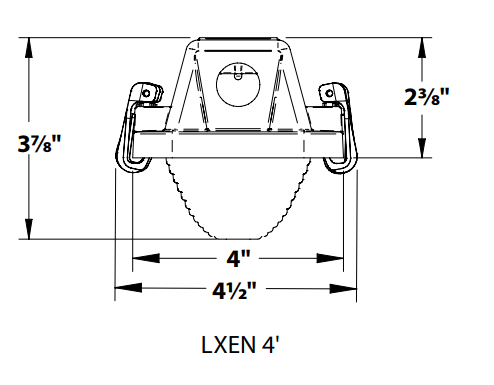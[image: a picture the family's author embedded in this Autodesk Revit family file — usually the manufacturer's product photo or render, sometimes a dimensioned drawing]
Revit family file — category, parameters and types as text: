
# Revit family: LXEN
name_source: partatom
category: Lighting Fixtures
revit_build: Autodesk Revit 2014 (Build: 20130308_1515(x64)
units: mm (PartAtom-declared; Revit-internal decimal feet)

## types (1)
- LXEN
    Apparent Load = 0 VA
    Backbox = White
    Certification = All luminaires are built to UL1598 and 2108
standards, and bear appropriate CSA labels.
Ingress protection IP65, IP66, and IP67 standard.
UL Sanitation Certified per NSF Standards. Wet
location labeling is standard. DLC® (DesignLights
Consortium) Qualified. Please refer to the DLC
website for specific product qualifications at
www.designlights.org. The DTS, Dimming Bypass
Module, is for emergency circuit control loads
including sensors and wireless systems listed to
UL924. See page 3 for wiring diagram. Link to
Dimming Bypass Module Specification sheet.
    Color Filter = 16777215
    Default Elevation = 4.0'
    Description = LXEN is a narrow, multi-functional enclosed LED product which serves rugged to severe conditions as well as food service areas. At only 4-1/2inch wide, LXEN provides a slim, linear profile, which fits easily into confined spaces, provides excellent illumination, and comes standard with the certifications required for rough service environments.
    Dimming Lamp Color Temperature Shift = <None>
    Driver = Fixed Output, 0-10 V Dimming
    Emit from Line Length = 2.0'
    Features = Available in 4' length
Narrow housing design for applications with limited space
Long life 60,000 hour LEDs at L80 for reduced maintenance
Four LED color choices
IP65 and IP67 standard
IP66 all sizes when ordered with standard polyacetal (POM) latches
Fiberglass housing with F1 weatherability rating, standard
Wet label
Gasket is non-porous to ensure seal
Impact modified acrylic lens equivalent to 100% DR
Lens firmly secured with captive tamper resistance ready polyacetal (POM) latches
Stainless steel latching optional
UL Sanitation certified to NSF standards
Includes surface mounting brackets
Operates from -40 ºC to 50 ºC as standard
Removable gear tray electrical access
Optional elevated ambient on most models
UL Sanitation certified to NSF standards
DLC® (DesignLights Consortium) Qualified - see www.designlights.org
Five year warranty (Terms and Conditions apply)
    Glass = White Glass
    Lamp = LED Lamp
    Lumen Output = Extra Low Watt, Low Watt
    Manufacturer = Columbia Lighting
    Model = LXEN
    Nominal Watts = 102 W
    Photometric Note = For more ies file please find the above link
    Photometric Web File = LXEN4-30LW-RFA-EDU.ies
    Photometric Web Link = https://www.hubbell.com
    Product Documentation Link = https://hubbellcdn.com
    Product Page URL = https://www.hubbell.com
    Row Length = 4.0'
    Shielding = Lineal ribbed frosted acrylic lens
    Tilt Angle = -90.00°
    URL = https://www.hubbell.com
    Voltage = 120 V
    Warranty = Five year warranty

## geometry (parser evidence)
native form markers: Blend x2, Sweep x3
no freeform markers — native parametric forms only
